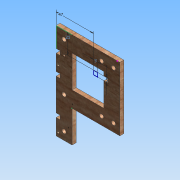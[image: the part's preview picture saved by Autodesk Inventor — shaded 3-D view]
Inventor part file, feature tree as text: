
AUTODESK INVENTOR PART (.ipt)
format: ipt  version: 2015 (Build 190159000, 159)  size: 270,336 bytes
history: native  units: mm
features: extrude x10, sketch x10, reference x7, projected_geometry x2
ambient origin geometry x8: Origin, YZ Plane, XZ Plane, XY Plane, X Axis, Y Axis, Z Axis, Center Point
bodies: Body1 (feature_tree)
feature tree (29):
  extrude  "Extrusion3"  Depth=20.0mm
  extrude  "Extrusion4"  Depth=10.0mm
  extrude  "Extrusion5"  Depth=5.0mm
  extrude  "Extrusion6"  Depth=10.0mm
  extrude  "Extrusion7"  Depth=60.0mm
  extrude  "Extrusion8"  Depth=40.0mm
  extrude  "Extrusion9"  Depth=10.0mm
  extrude  "Extrusion10"  Depth=40.0mm
  sketch  "Sketch12"  dims[d19=10.0mm d20=40.0mm]
  extrude  "Extrusion14"  Depth=10.0mm
  extrude  "Extrusion15"  Depth=5.0mm TaperAngle=0.0deg
  sketch  "Sketch5"  dims[d0=80.0mm d3=20.0mm]
  reference  "Reference1"
  reference  "Reference2"
  projected_geometry  "Projected Loop1"
  sketch  "Sketch6"  dims[d4=5.0mm d5=10.0mm]
  sketch  "Sketch7"  dims[d6=10.0mm d7=5.0mm]
  sketch  "Sketch8"  dims[d8=10.0mm d9=10.0mm]
  sketch  "Sketch9"  dims[d12=5.0mm d13=60.0mm]
  sketch  "Sketch10"  dims[d14=5.0mm d15=0.0mm d16=40.0mm]
  reference  "Reference3"
  reference  "Reference4"
  reference  "Reference5"
  sketch  "Sketch11"  dims[d17=5.0mm d18=10.0mm]
  sketch  "Sketch15"  dims[d21=5.0mm d22=10.0mm]
  reference  "Reference6"
  reference  "Reference7"
  projected_geometry  "Projected Loop3"
  sketch  "Sketch16"  dims[d23=10.0mm d24=5.0mm d25=0.0mm d26=5.0mm d27=5.0mm d28=20.0mm d29=5.0mm d30=5.0mm d31=40.0mm d32=10.0mm d33=0.0mm d34=2.0mm d35=10.0mm d36=92.5mm d37=92.5mm d38=0.0mm d39=2.0mm d40=2.5mm d41=5.0mm d42=10.0mm d43=0.0mm d44=2.0mm d45=2.5mm d46=8.0mm d47=10.0mm d48=0.0mm d49=5.0mm d50=0.0mm d51=5.0mm d52=5.0mm d53=25.0mm d54=5.0mm d55=0.0mm d56=5.0mm d57=5.0mm d58=47.0mm d59=25.0mm d69=20.0mm d70=80.0mm d71=20.0mm d72=80.0mm d73=5.0mm d74=5.0mm d75=8.0mm d76=23.0mm d77=5.0mm d78=5.0mm d79=8.0mm d80=23.0mm d81=10.0mm d82=10.0mm d83=5.0mm d84=0.0mm d85=5.0mm d86=5.0mm d87=25.0mm d88=5.0mm d89=0.0mm d90=20.0mm]
